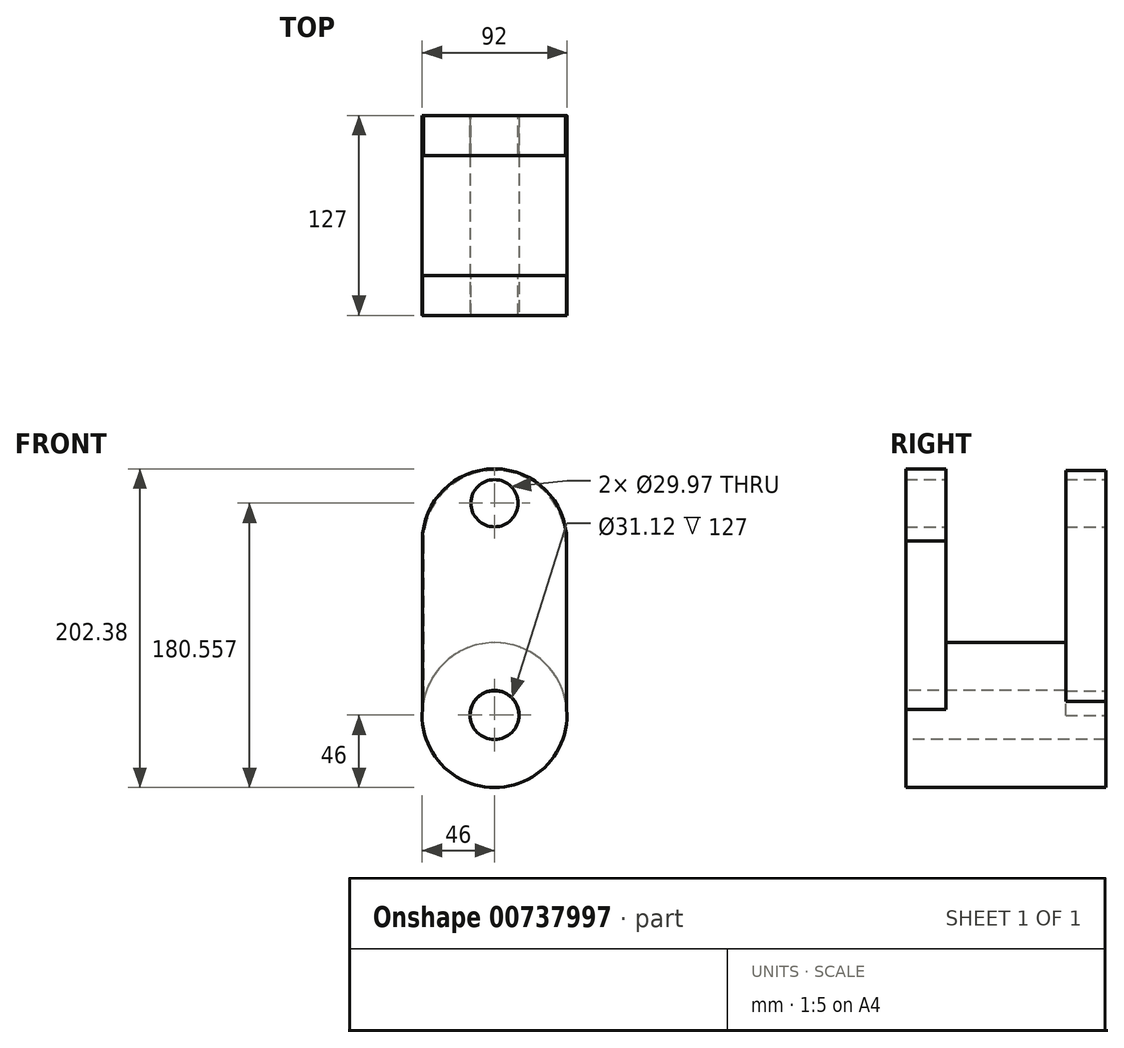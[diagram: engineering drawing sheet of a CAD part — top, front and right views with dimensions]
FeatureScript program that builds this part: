
annotation { "Feature Type Name" : "Feature", "Feature Type Description" : "" }
export const myFeature = defineFeature(function(context is Context, id is Id, definition is map)
    precondition{}
    {
        {
            var Q0;
            Q0=qCreatedBy(makeId("Front.planeOp"),FACE);
            var sketch = newSketch(context, id + "F0", { "sketchPlane" : qUnion([Q0])});
            skCircle(sketch, "E0", {"center": v(0, 0) * mm, "radius": 46 * mm});
            skSolve(sketch);
        }
        {
            var Q0;
            Q0=makeQuery(id+"F0.imprint","IMPRINT",FACE,{"disambiguationData":[TD([[makeQuery(id+"F0.imprint","IMPRINT",EDGE,{"derivedFrom":sQuery(id+"F0.wireOp",EDGE,"E0")}),1.0]])]});
            extrude(context, id + "F1", {"entities" : qUnion([Q0]), "depth" : 127 * mm, "offsetDistance" : 25.4 * mm});
        }
        {
            var Q0;
            Q0=qCreatedBy(makeId("Front.planeOp"),FACE);
            var sketch = newSketch(context, id + "F2", { "sketchPlane" : qUnion([Q0])});
            skCircle(sketch, "E1", {"center": v(0, 0) * mm, "radius": 15.51 * mm});
            skSolve(sketch);
        }
        {
            var Q0;
            Q0 = qSketchRegion(id + "F2", true);
            extrude(context, id + "F3", {"entities" : qUnion([Q0]), "operationType" : NewBodyOperationType.REMOVE, "depth" : 127 * mm, "offsetDistance" : 25.4 * mm});
        }
        {
            var Q0;
            Q0=makeQuery(id+"F1.opExtrude","CAP_FACE",FACE,{"disambiguationData":[OSD([sQuery(id+"F0.wireOp",EDGE,"E0")])],"isStart":false});
            var sketch = newSketch(context, id + "F4", { "sketchPlane" : qUnion([Q0])});
            skLineSegment(sketch, "E2.bottom", {"start": v(45.86, 110.58) * mm, "end": v(-45.86, 110.58) * mm});
            skLineSegment(sketch, "E2.top", {"start": v(45.86, 0.23) * mm, "end": v(-45.86, 0.23) * mm});
            skLineSegment(sketch, "E2.left", {"start": v(45.86, 110.58) * mm, "end": v(45.86, 0.23) * mm});
            skLineSegment(sketch, "E2.right", {"start": v(-45.86, 110.58) * mm, "end": v(-45.86, 0.23) * mm});
            skPoint(sketch, "E2.middle", {"position": v(0, 55.4) * mm});
            skSolve(sketch);
        }
        {
            var Q0;
            Q0 = qSketchRegion(id + "F4", true);
            extrude(context, id + "F5", {"entities" : qUnion([Q0]), "operationType" : NewBodyOperationType.ADD, "oppositeDirection" : true, "depth" : 25.4 * mm, "offsetDistance" : 25.4 * mm});
        }
        {
            var Q0;
            Q0=makeQuery(id+"F5.boolean.opBoolean","MERGE",FACE,{"derivedFrom":[makeQuery(id+"F1.opExtrude","CAP_FACE",FACE,{"disambiguationData":[OSD([sQuery(id+"F0.wireOp",EDGE,"E0")])],"isStart":false}),makeQuery(id+"F5.opExtrude","CAP_FACE",FACE,{"disambiguationData":[OSD([sQuery(id+"F4.wireOp",EDGE,"E2.bottom"),sQuery(id+"F4.wireOp",EDGE,"E2.top"),sQuery(id+"F4.wireOp",EDGE,"E2.left"),sQuery(id+"F4.wireOp",EDGE,"E2.right")])],"isStart":true})]});
            var sketch = newSketch(context, id + "F6", { "sketchPlane" : qUnion([Q0])});
            skCircle(sketch, "E3", {"center": v(0, 0) * mm, "radius": 15.56 * mm});
            skSolve(sketch);
        }
        {
            var Q0;
            Q0 = qSketchRegion(id + "F6", true);
            extrude(context, id + "F7", {"entities" : qUnion([Q0]), "operationType" : NewBodyOperationType.REMOVE, "oppositeDirection" : true, "depth" : 127 * mm, "offsetDistance" : 25.4 * mm});
        }
        {
            var Q0;
            Q0=makeQuery(id+"F5.boolean.opBoolean","MERGE",FACE,{"derivedFrom":[makeQuery(id+"F1.opExtrude","CAP_FACE",FACE,{"disambiguationData":[OSD([sQuery(id+"F0.wireOp",EDGE,"E0")])],"isStart":false}),makeQuery(id+"F5.opExtrude","CAP_FACE",FACE,{"disambiguationData":[OSD([sQuery(id+"F4.wireOp",EDGE,"E2.bottom"),sQuery(id+"F4.wireOp",EDGE,"E2.top"),sQuery(id+"F4.wireOp",EDGE,"E2.left"),sQuery(id+"F4.wireOp",EDGE,"E2.right")])],"isStart":true})]});
            var sketch = newSketch(context, id + "F8", { "sketchPlane" : qUnion([Q0])});
            skCircle(sketch, "E4", {"center": v(0, 110.58) * mm, "radius": 45.8 * mm});
            skSolve(sketch);
        }
        {
            var Q0;
            Q0 = qSketchRegion(id + "F8", true);
            extrude(context, id + "F9", {"entities" : qUnion([Q0]), "operationType" : NewBodyOperationType.ADD, "oppositeDirection" : true, "depth" : 25.4 * mm, "offsetDistance" : 25.4 * mm});
        }
        {
            var Q0;
            Q0=makeQuery(id+"F1.opExtrude","CAP_FACE",FACE,{"disambiguationData":[OSD([sQuery(id+"F0.wireOp",EDGE,"E0")])],"isStart":true});
            var sketch = newSketch(context, id + "F10", { "sketchPlane" : qUnion([Q0])});
            skLineSegment(sketch, "E5.bottom", {"start": v(45.14, 110.22) * mm, "end": v(-45.14, 110.22) * mm});
            skLineSegment(sketch, "E5.top", {"start": v(45.14, -0.3) * mm, "end": v(-45.14, -0.3) * mm});
            skLineSegment(sketch, "E5.left", {"start": v(45.14, 110.22) * mm, "end": v(45.14, -0.3) * mm});
            skLineSegment(sketch, "E5.right", {"start": v(-45.14, 110.22) * mm, "end": v(-45.14, -0.3) * mm});
            skPoint(sketch, "E5.middle", {"position": v(0, 54.97) * mm});
            skSolve(sketch);
        }
        {
            var Q0;
            Q0 = qSketchRegion(id + "F10", true);
            extrude(context, id + "F11", {"entities" : qUnion([Q0]), "operationType" : NewBodyOperationType.ADD, "oppositeDirection" : true, "depth" : 25.4 * mm, "offsetDistance" : 25.4 * mm});
        }
        {
            var Q0;
            Q0=makeQuery(id+"F11.boolean.opBoolean","MERGE",FACE,{"derivedFrom":[makeQuery(id+"F1.opExtrude","CAP_FACE",FACE,{"disambiguationData":[OSD([sQuery(id+"F0.wireOp",EDGE,"E0")])],"isStart":true}),makeQuery(id+"F11.opExtrude","CAP_FACE",FACE,{"disambiguationData":[OSD([sQuery(id+"F10.wireOp",EDGE,"E5.bottom"),sQuery(id+"F10.wireOp",EDGE,"E5.top"),sQuery(id+"F10.wireOp",EDGE,"E5.left"),sQuery(id+"F10.wireOp",EDGE,"E5.right")])],"isStart":true})]});
            var sketch = newSketch(context, id + "F12", { "sketchPlane" : qUnion([Q0])});
            skCircle(sketch, "E6", {"center": v(0, 0) * mm, "radius": 15.46 * mm});
            skSolve(sketch);
        }
        {
            var Q0;
            Q0 = qSketchRegion(id + "F12", true);
            extrude(context, id + "F13", {"entities" : qUnion([Q0]), "operationType" : NewBodyOperationType.REMOVE, "oppositeDirection" : true, "depth" : 127 * mm, "offsetDistance" : 25.4 * mm});
        }
        {
            var Q0;
            Q0=makeQuery(id+"F11.boolean.opBoolean","MERGE",FACE,{"derivedFrom":[makeQuery(id+"F1.opExtrude","CAP_FACE",FACE,{"disambiguationData":[OSD([sQuery(id+"F0.wireOp",EDGE,"E0")])],"isStart":true}),makeQuery(id+"F11.opExtrude","CAP_FACE",FACE,{"disambiguationData":[OSD([sQuery(id+"F10.wireOp",EDGE,"E5.bottom"),sQuery(id+"F10.wireOp",EDGE,"E5.top"),sQuery(id+"F10.wireOp",EDGE,"E5.left"),sQuery(id+"F10.wireOp",EDGE,"E5.right")])],"isStart":true})]});
            var sketch = newSketch(context, id + "F14", { "sketchPlane" : qUnion([Q0])});
            skCircle(sketch, "E7", {"center": v(0, 110.22) * mm, "radius": 45.14 * mm});
            skSolve(sketch);
        }
        {
            var Q0;
            {var subQ1=makeQuery(id+"F11.opExtrude","CAP_EDGE",EDGE,{"disambiguationData":[OSD([sQuery(id+"F10.wireOp",EDGE,"E5.bottom")])],"isStart":true});Q0=makeQuery(id+"F14.imprint","IMPRINT",FACE,{"disambiguationData":[TD([[makeQuery(id+"F14.imprint","IMPRINT",EDGE,{"derivedFrom":subQ1}),-1.0]])]});}
            var Q1;
            Q1=sQuery(id+"F14.wireOp",EDGE,"E7");
            extrude(context, id + "F15", {"entities" : qUnion([Q0]), "operationType" : NewBodyOperationType.ADD, "surfaceEntities" : qUnion([Q1]), "oppositeDirection" : true, "depth" : 25.4 * mm, "offsetDistance" : 25.4 * mm});
        }
        {
            var Q0;
            {var subQ0=sQuery(id+"F10.wireOp",EDGE,"E5.bottom");Q0=makeQuery(id+"F15.boolean.opBoolean","MERGE",FACE,{"derivedFrom":[makeQuery(id+"F11.boolean.opBoolean","MERGE",FACE,{"derivedFrom":[makeQuery(id+"F1.opExtrude","CAP_FACE",FACE,{"disambiguationData":[OSD([sQuery(id+"F0.wireOp",EDGE,"E0")])],"isStart":true}),makeQuery(id+"F11.opExtrude","CAP_FACE",FACE,{"disambiguationData":[OSD([subQ0,sQuery(id+"F10.wireOp",EDGE,"E5.top"),sQuery(id+"F10.wireOp",EDGE,"E5.left"),sQuery(id+"F10.wireOp",EDGE,"E5.right")])],"isStart":true})]}),makeQuery(id+"F15.opExtrude","CAP_FACE",FACE,{"disambiguationData":[OSD([subQ0,sQuery(id+"F14.wireOp",EDGE,"E7")])],"isStart":true})]});}
            var sketch = newSketch(context, id + "F16", { "sketchPlane" : qUnion([Q0])});
            skCircle(sketch, "E8", {"center": v(0, 134.56) * mm, "radius": 14.99 * mm});
            skPoint(sketch, "E8.centerSnap0", {"position": v(0, 155.37) * mm});
            skSolve(sketch);
        }
        {
            var Q0;
            Q0 = qSketchRegion(id + "F16", true);
            extrude(context, id + "F17", {"entities" : qUnion([Q0]), "operationType" : NewBodyOperationType.REMOVE, "oppositeDirection" : true, "depth" : 127 * mm, "offsetDistance" : 25.4 * mm});
        }
    });
